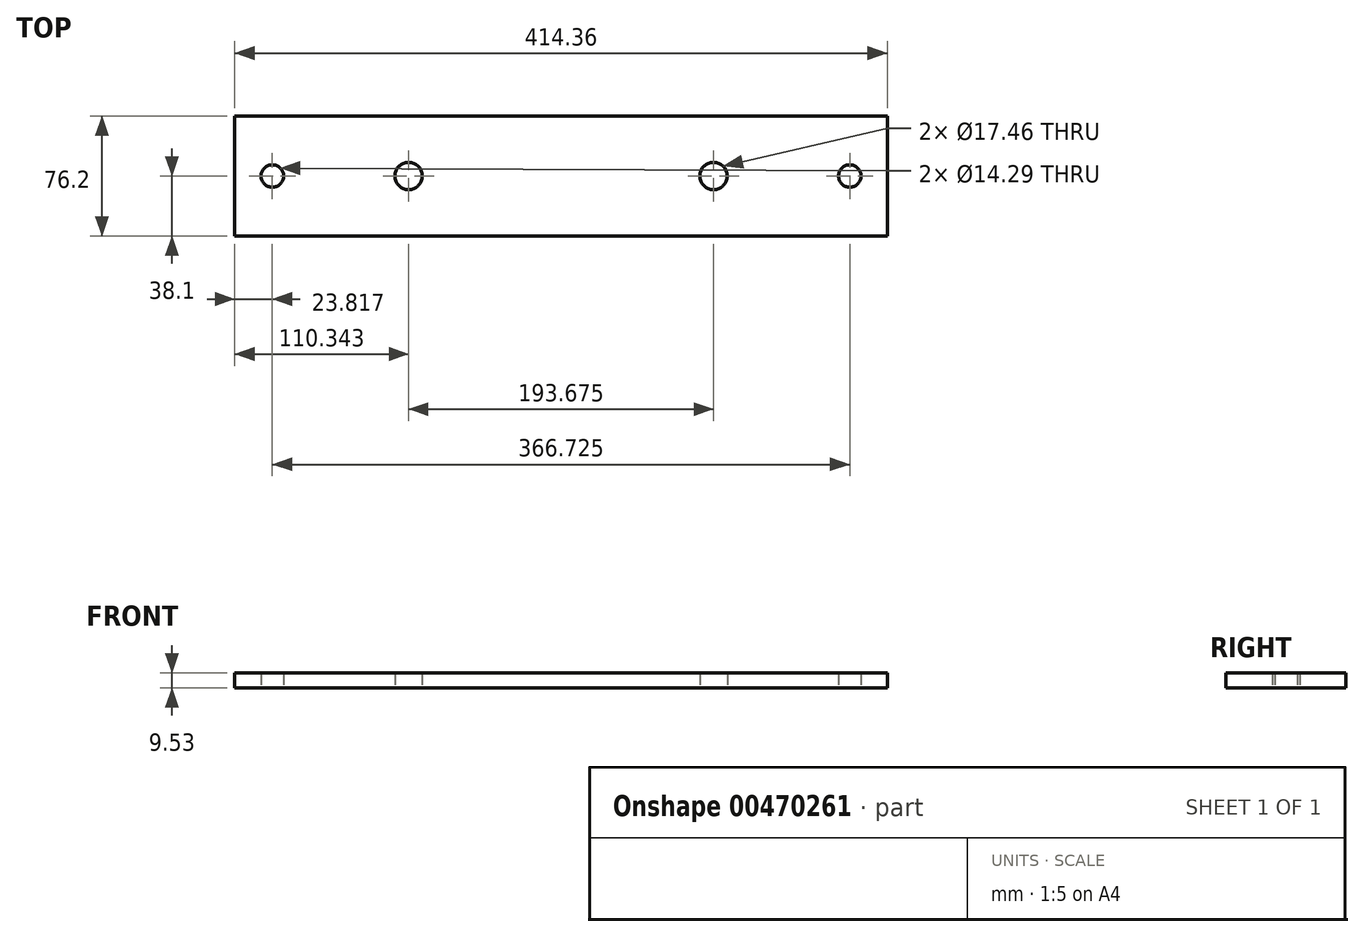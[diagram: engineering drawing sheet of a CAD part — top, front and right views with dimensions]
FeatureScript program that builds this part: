
annotation { "Feature Type Name" : "Feature", "Feature Type Description" : "" }
export const myFeature = defineFeature(function(context is Context, id is Id, definition is map)
    precondition{}
    {
        {
            var Q0;
            Q0=qCreatedBy(makeId("Top.planeOp"),FACE);
            var sketch = newSketch(context, id + "F0", { "sketchPlane" : qUnion([Q0])});
            skLineSegment(sketch, "E0.bottom", {"start": v(207.18, -38.1) * mm, "end": v(-207.18, -38.1) * mm});
            skLineSegment(sketch, "E0.top", {"start": v(207.18, 38.1) * mm, "end": v(-207.18, 38.1) * mm});
            skLineSegment(sketch, "E0.left", {"start": v(207.18, -38.1) * mm, "end": v(207.18, 38.1) * mm});
            skLineSegment(sketch, "E0.right", {"start": v(-207.18, -38.1) * mm, "end": v(-207.18, 38.1) * mm});
            skPoint(sketch, "E0.middle", {"position": v(0, 0) * mm});
            skCircle(sketch, "E1", {"center": v(-96.84, 0) * mm, "radius": 8.73 * mm});
            skCircle(sketch, "E2", {"center": v(-183.36, 0) * mm, "radius": 7.14 * mm});
            skPoint(sketch, "E2.centerSnap0", {"position": v(-207.18, 0) * mm});
            skCircle(sketch, "E3.MirrorC", {"center": v(96.84, 0) * mm, "radius": 8.73 * mm});
            skCircle(sketch, "E4.MirrorC", {"center": v(183.36, 0) * mm, "radius": 7.14 * mm});
            skSolve(sketch);
        }
        {
            var Q0;
            Q0 = qSketchRegion(id + "F0", true);
            extrude(context, id + "F1", {"entities" : qUnion([Q0]), "depth" : 9.52 * mm});
        }
    });
